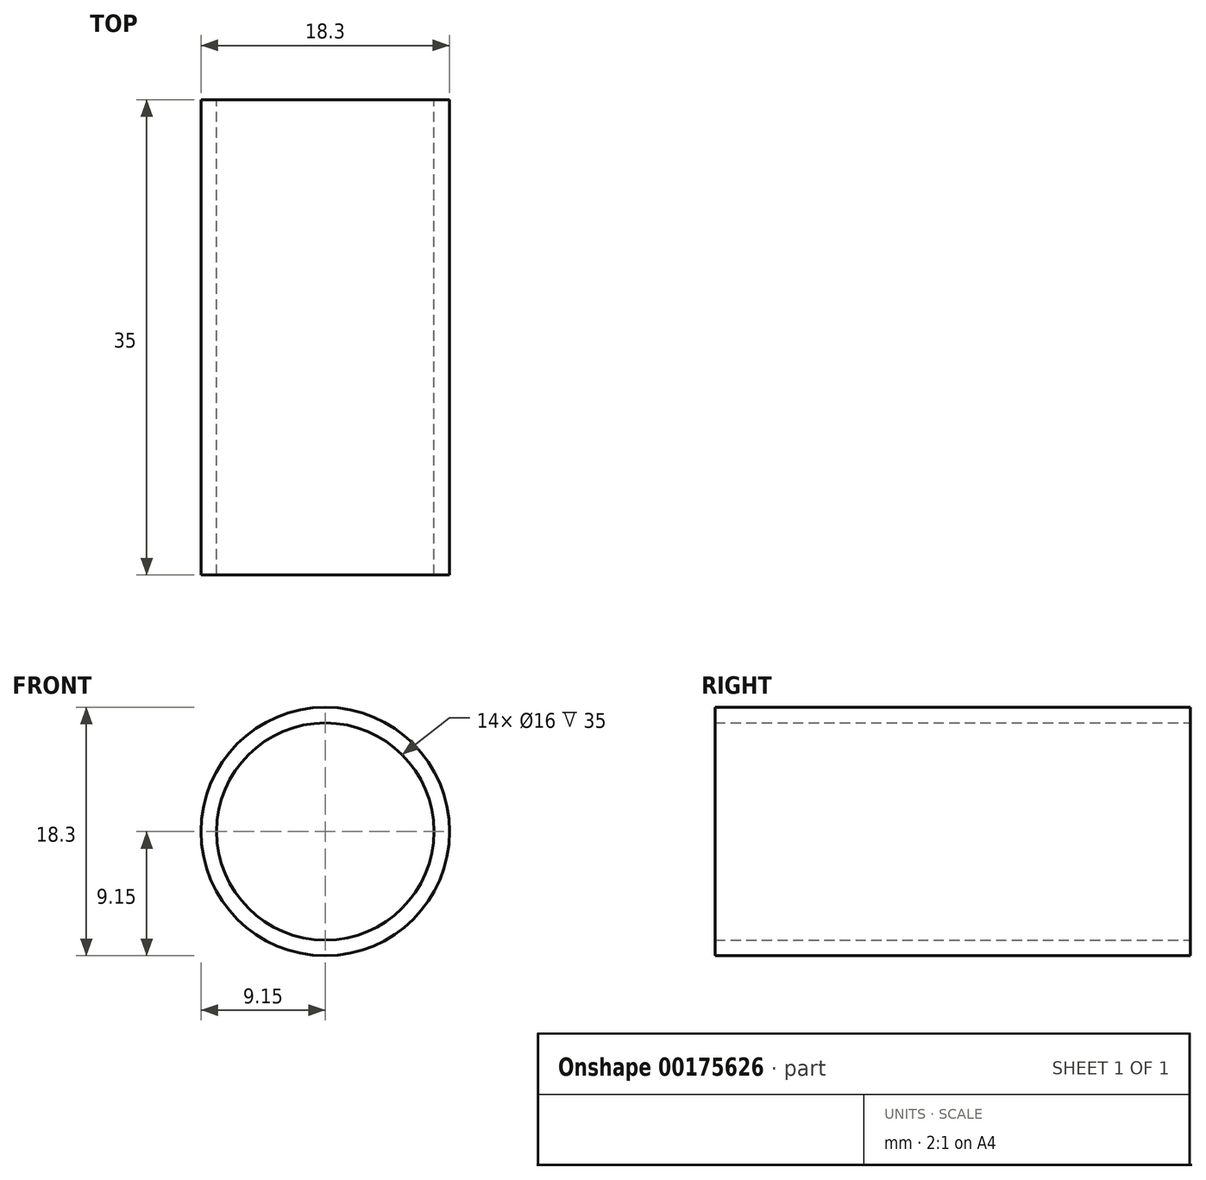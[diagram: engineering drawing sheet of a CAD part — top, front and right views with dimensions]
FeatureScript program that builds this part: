
annotation { "Feature Type Name" : "Feature", "Feature Type Description" : "" }
export const myFeature = defineFeature(function(context is Context, id is Id, definition is map)
    precondition{}
    {
        {
            var Q0;
            Q0=qCreatedBy(makeId("Front.planeOp"),FACE);
            var sketch = newSketch(context, id + "F0", { "sketchPlane" : qUnion([Q0])});
            skCircle(sketch, "E0", {"center": v(0, 0) * mm, "radius": 9.15 * mm});
            skCircle(sketch, "E1", {"center": v(0, 0) * mm, "radius": 8 * mm});
            skSolve(sketch);
        }
        {
            var Q0;
            Q0 = qSketchRegion(id + "F0", true);
            extrude(context, id + "F1", {"entities" : qUnion([Q0]), "depth" : 35 * mm});
        }
    });
